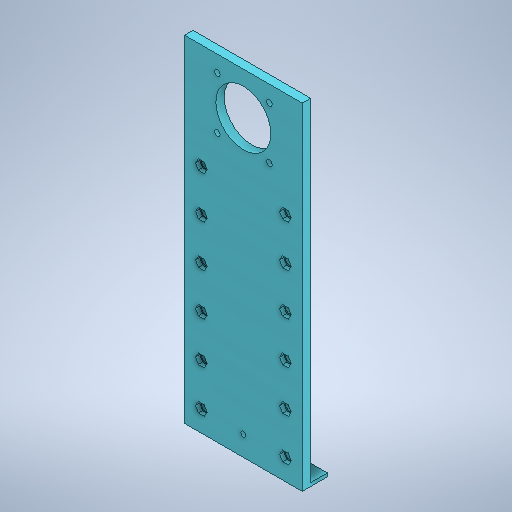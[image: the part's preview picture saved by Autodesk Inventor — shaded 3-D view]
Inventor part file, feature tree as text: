
AUTODESK INVENTOR PART (.ipt)
format: ipt  version: 2025.1 (Build 291241000, 241)  size: 415,744 bytes
history: native  units: mm
features: sketch x5, extrude x4, other x3, pattern_linear x1, mirror x1, hole x1, fillet x1
ambient origin geometry x8: Origin, YZ Plane, XZ Plane, XY Plane, X Axis, Y Axis, Z Axis, Center Point
bodies: Solide1 (feature_tree)
feature tree (16):
  extrude  "Extrusion1"  Depth=200.0mm
  extrude  "Extrusion3"  Depth=70.0mm
  pattern_linear  "Réseau rectangulaire1"  Spacing1=35.0mm  [1 undecoded]
  other  "Plan de construction1"
  mirror  "Mise en miroir1"
  extrude  "Extrusion5"  Depth=15.5mm
  hole  "Perçage4"  [1 undecoded]
  extrude  "Extrusion6"  Depth=5.0mm TaperAngle=0.0deg
  fillet  "Congé4"  Radius=6.0mm
  sketch  "Esquisse1"
  other  "Réseau d'esquisse rectangulaire2"
  sketch  "Esquisse4"
  other  "Réseau d'esquisse rectangulaire3"
  sketch  "Esquisse7"
  sketch  "Esquisse9"
  sketch  "Esquisse10"
note: 2 required parameter values undecoded (feature->parameter linkage not recoverable at this tier; creation-order binding heuristic only, values carry confidence <= 0.55)
